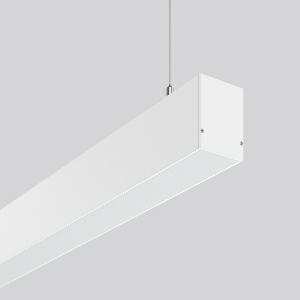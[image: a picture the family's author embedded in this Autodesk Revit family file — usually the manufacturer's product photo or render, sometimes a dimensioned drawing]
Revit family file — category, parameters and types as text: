
# Revit family: less_is_more_50_312315_002_e754
name_source: partatom
category: Lighting Fixtures
units: mm (PartAtom-declared; Revit-internal decimal feet)

## family parameters
Cut with Voids When Loaded = No
Host = Face
Light Source = No
Part Type = Normal
Room Calculation Point = No
Round Connector Dimension = Use Diameter
Shared = No

## types (1)
- LESS IS MORE 50 (1 x LED Modul 830, 5400 lm, 3000)
    Apparent Load = 47 VA
    CIE Flux Codes = 48 79 95 100 100
    Color Rendering = 80
    Color Temperature = 3000
    Default Elevation = 1800 mm
    Description = Series: LESS IS MORE 50
Linear pendant luminaire for aesthetically sophisticated lighting. Housing: extruded aluminium profile, powder-coated. End cap aluminium powder-coated. Canopy made of aluminium, powder-coated. Diffuser made of non-yellowing plastic (PMMA), opal. Direct light emission. Suitable for pendant. 2-point steel cable suspension freely positionable and infinitely height-adjustable. Special lengths available on request. LED unit with integrated converter interchangeable and removable. Suitable for through-wiring. With sensors or as a safety luminaire on request. 
Colour: traffic white, matt (RAL 9016)
Length: 1967 mm
Width: 57 mm
Height: 75 mm
Suspension length: 2000 mm
Lamp: LED
Socket: without socket
Colour temperature: 3000K
Colour rendering index (CRI): 80
System power: 47 W
Rated luminous flux: 5400 lm
Luminous efficiency: 115 lm/W
Control gear: Regulated power supply
Protection class: I
Type of protection: IP 20
    Height = 75 mm
    Lamp = 1 x LED Modul 830
    Lamp Light Flux = 5400 lm
    Lamp count = 1
    Length = 1967 mm
    Lifetime = 50000 h
    Luminous efficacy = 115 lm/W
    Manufacturer = RZB
    ModVariant = No
    Model = 312315.002
    Mounting Place = Ceiling
    Mounting Type = Pendant
    Number of Poles = 1
    OnlyDefault = Yes
    Power Factor = 1
    Product Name = LESS IS MORE 50
    Product group = Pendant LED linear luminaires
    ProductGroupID = 907
    Protection Class = Protection class I
    Protection Degree = IP 20
    RLX_Detail_Level = 1
    RLX_Emergency_Light_Flux = 0 lm
    RLX_Emergency_Type = 0
    RLX_Emergency_Type_DB = No
    RlxData = <blob elided: 20605 chars, md5=eba48a8f>
    Socket = socket
    Standby Power = 0 W
    System Light Flux = 5400 lm
    System Power = 47 W
    Type Comments = Product without accessories
    Type Image = 312318.002.jpg
    URL = http://relux.com
    VarID = ---
    Voltage = 230 V
    Voltage Range = 220-240 V
    Weight = 0.00 kg
    Width = 57 mm

## geometry (parser evidence)
native form markers: Blend x4, Sweep x10
no freeform markers — native parametric forms only
